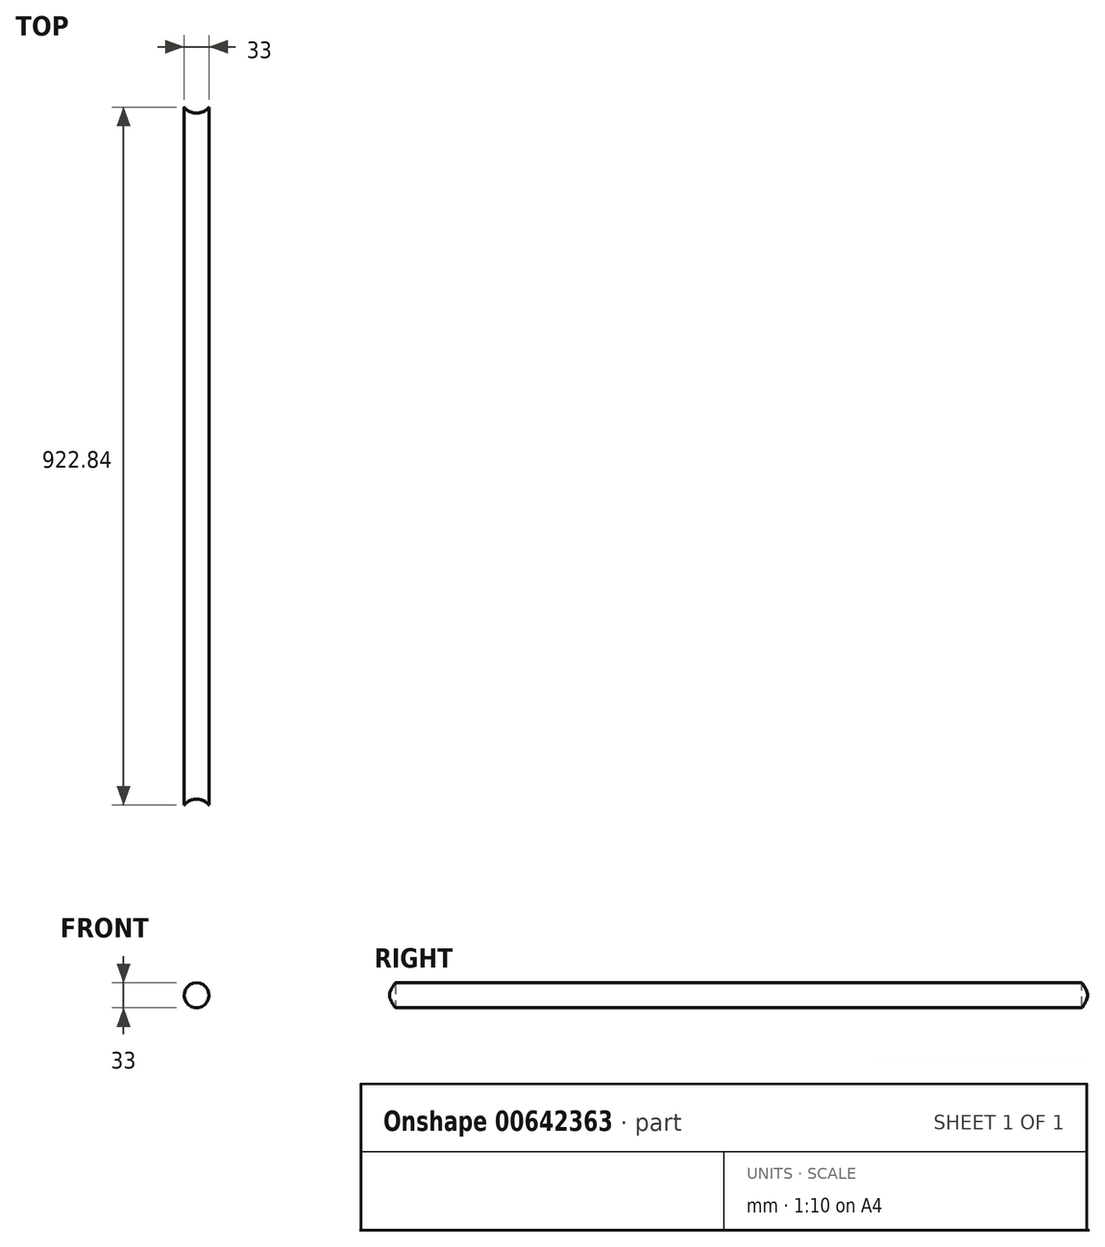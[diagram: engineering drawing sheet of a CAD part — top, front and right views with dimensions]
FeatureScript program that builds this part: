
annotation { "Feature Type Name" : "Feature", "Feature Type Description" : "" }
export const myFeature = defineFeature(function(context is Context, id is Id, definition is map)
    precondition{}
    {
        {
            var Q0;
            Q0=qCreatedBy(makeId("Front.planeOp"),FACE);
            var sketch = newSketch(context, id + "F0", { "sketchPlane" : qUnion([Q0])});
            skCircle(sketch, "E0", {"center": v(0, 0) * mm, "radius": 16.5 * mm});
            skSolve(sketch);
        }
        {
            var Q0;
            Q0=makeQuery(id+"F0.imprint","IMPRINT",FACE,{"disambiguationData":[TD([[makeQuery(id+"F0.imprint","IMPRINT",EDGE,{"derivedFrom":sQuery(id+"F0.wireOp",EDGE,"E0")}),1.0]])]});
            extrude(context, id + "F1", {"entities" : qUnion([Q0]), "depth" : 945 * mm, "offsetDistance" : 25 * mm});
        }
        {
            var Q0;
            Q0=qCreatedBy(makeId("Top.planeOp"),FACE);
            var sketch = newSketch(context, id + "F2", { "sketchPlane" : qUnion([Q0])});
            skLineSegment(sketch, "E1", {"start": v(-21, 0) * mm, "end": v(0, 0) * mm});
            skLineSegment(sketch, "E2", {"start": v(0, 0) * mm, "end": v(21, 0) * mm});
            skArc(sketch, "E3", {"start": v(-21, 0) * mm, "mid": v(0, -16.9) * mm, "end": v(21, 0) * mm});
            skSolve(sketch);
        }
        {
            var Q0;
            Q0=qSketchRegion(id+"F2",true);
            extrude(context, id + "F3", {"entities" : qUnion([Q0]), "operationType" : NewBodyOperationType.REMOVE, "endBound" : BoundingType.SYMMETRIC, "oppositeDirection" : true, "depth" : 1000 * mm, "offsetDistance" : 25 * mm});
        }
        {
            var Q0;
            Q0=qCreatedBy(makeId("Top.planeOp"),FACE);
            var sketch = newSketch(context, id + "F4", { "sketchPlane" : qUnion([Q0])});
            skArc(sketch, "E4", {"start": v(21, -945) * mm, "mid": v(0, -924) * mm, "end": v(-21, -945) * mm});
            skLineSegment(sketch, "E5", {"start": v(-21, -945) * mm, "end": v(21, -945) * mm});
            skSolve(sketch);
        }
        {
            var Q0;
            Q0=qSketchRegion(id+"F4",true);
            extrude(context, id + "F5", {"entities" : qUnion([Q0]), "operationType" : NewBodyOperationType.REMOVE, "endBound" : BoundingType.SYMMETRIC, "depth" : 100 * mm, "offsetDistance" : 25 * mm});
        }
    });
